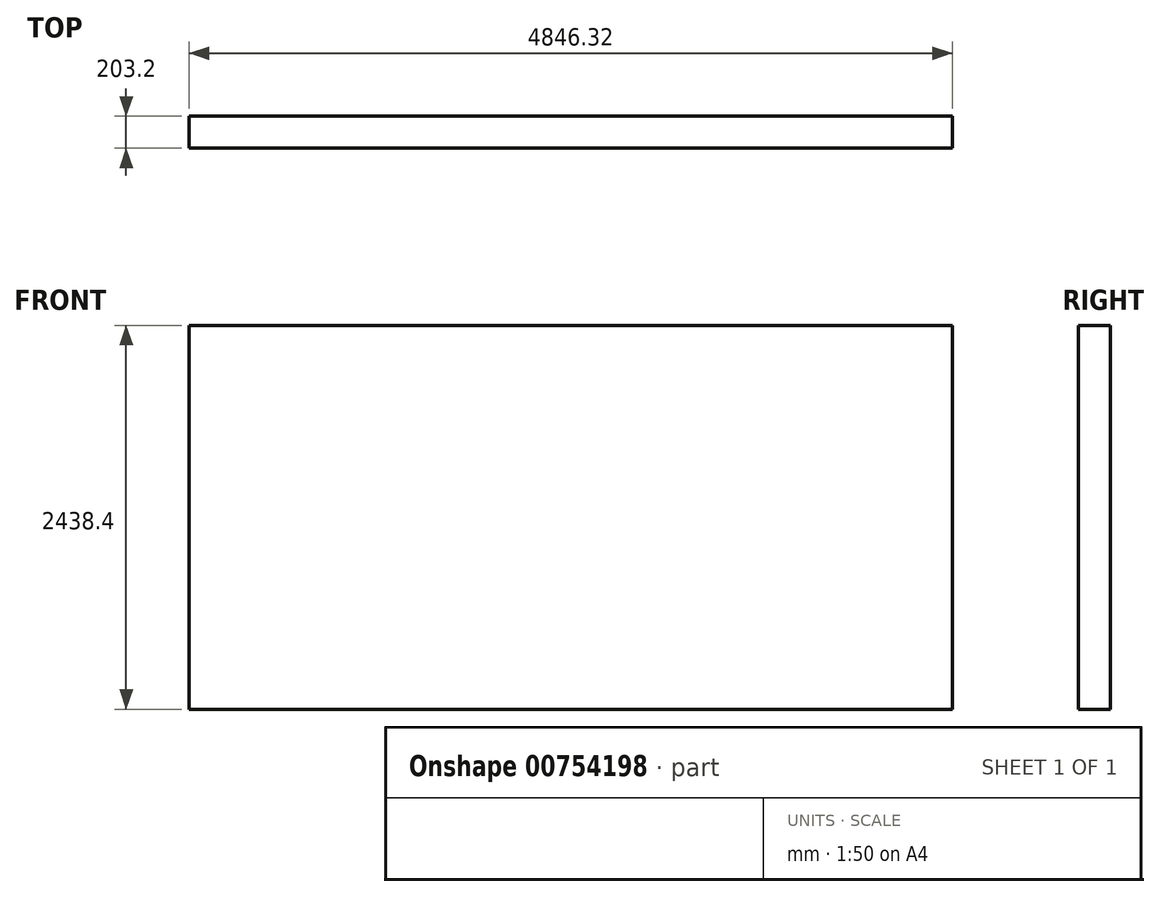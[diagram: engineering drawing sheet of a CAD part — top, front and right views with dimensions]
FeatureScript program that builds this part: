
annotation { "Feature Type Name" : "Feature", "Feature Type Description" : "" }
export const myFeature = defineFeature(function(context is Context, id is Id, definition is map)
    precondition{}
    {
        {
            var Q0;
            Q0=qCreatedBy(makeId("Front.planeOp"),FACE);
            var sketch = newSketch(context, id + "F0", { "sketchPlane" : qUnion([Q0])});
            skLineSegment(sketch, "E0.bottom", {"start": v(2423.16, 1219.2) * mm, "end": v(-2423.16, 1219.2) * mm});
            skLineSegment(sketch, "E0.top", {"start": v(2423.16, -1219.2) * mm, "end": v(-2423.16, -1219.2) * mm});
            skLineSegment(sketch, "E0.left", {"start": v(2423.16, 1219.2) * mm, "end": v(2423.16, -1219.2) * mm});
            skLineSegment(sketch, "E0.right", {"start": v(-2423.16, 1219.2) * mm, "end": v(-2423.16, -1219.2) * mm});
            skPoint(sketch, "E0.middle", {"position": v(0, 0) * mm});
            skSolve(sketch);
        }
        {
            var Q0;
            Q0=makeQuery(id+"F0.imprint","IMPRINT",FACE,{"disambiguationData":[TD([[makeQuery(id+"F0.imprint","IMPRINT",EDGE,{"derivedFrom":sQuery(id+"F0.wireOp",EDGE,"E0.bottom")}),1.0]])]});
            extrude(context, id + "F1", {"entities" : qUnion([Q0]), "depth" : 203.2 * mm, "offsetDistance" : 25.4 * mm});
        }
    });
